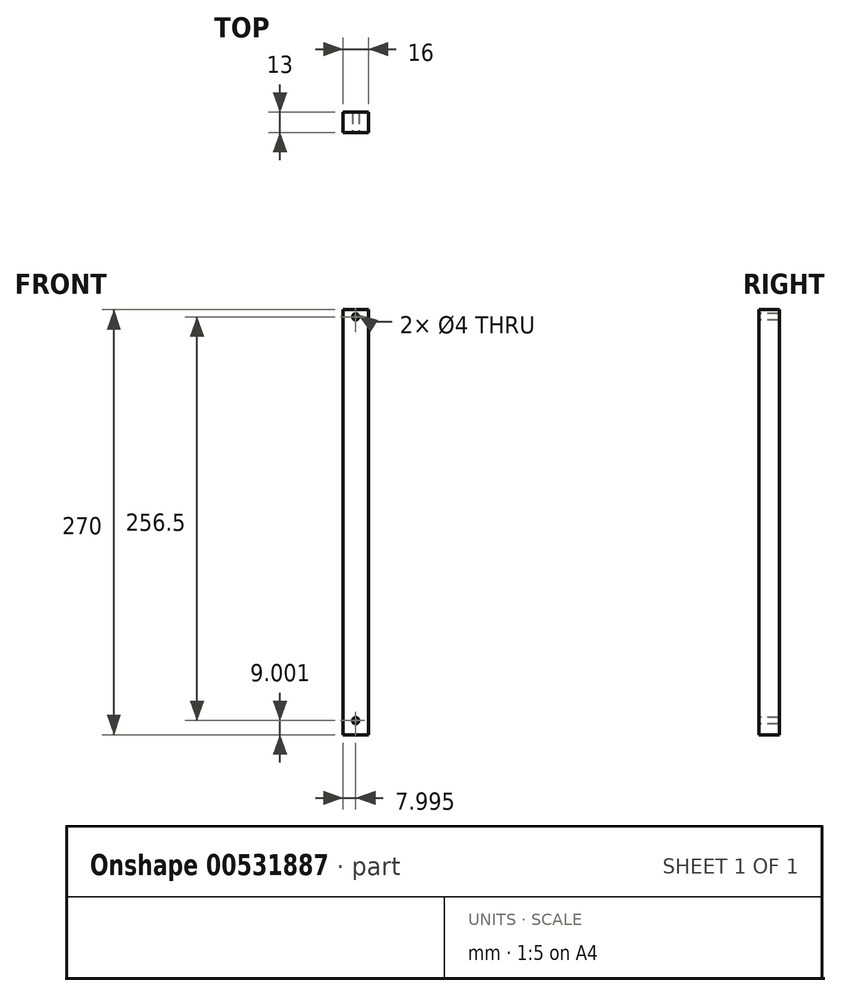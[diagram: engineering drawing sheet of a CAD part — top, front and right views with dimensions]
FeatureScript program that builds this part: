
annotation { "Feature Type Name" : "Feature", "Feature Type Description" : "" }
export const myFeature = defineFeature(function(context is Context, id is Id, definition is map)
    precondition{}
    {
        {
            var Q0;
            Q0=qCreatedBy(makeId("Front.planeOp"),FACE);
            var sketch = newSketch(context, id + "F0", { "sketchPlane" : qUnion([Q0])});
            skLineSegment(sketch, "E0.bottom", {"start": v(-46.2, 242.17) * mm, "end": v(-30.2, 242.17) * mm});
            skLineSegment(sketch, "E0.top", {"start": v(-46.2, -27.83) * mm, "end": v(-30.2, -27.83) * mm});
            skLineSegment(sketch, "E0.left", {"start": v(-46.2, 242.17) * mm, "end": v(-46.2, -27.83) * mm});
            skLineSegment(sketch, "E0.right", {"start": v(-30.2, 242.17) * mm, "end": v(-30.2, -27.83) * mm});
            skSolve(sketch);
        }
        {
            var Q0;
            Q0 = qSketchRegion(id + "F0", true);
            extrude(context, id + "F1", {"entities" : qUnion([Q0]), "depth" : 13 * mm, "offsetDistance" : 25 * mm});
        }
        {
            var Q0;
            Q0=makeQuery(id+"F1.opExtrude","CAP_FACE",FACE,{"disambiguationData":[OSD([sQuery(id+"F0.wireOp",EDGE,"E0.bottom"),sQuery(id+"F0.wireOp",EDGE,"E0.top"),sQuery(id+"F0.wireOp",EDGE,"E0.left"),sQuery(id+"F0.wireOp",EDGE,"E0.right")])],"isStart":false});
            var sketch = newSketch(context, id + "F2", { "sketchPlane" : qUnion([Q0])});
            skCircle(sketch, "E1", {"center": v(-38.2, -18.83) * mm, "radius": 2 * mm});
            skSolve(sketch);
        }
        {
            var Q0;
            Q0 = qSketchRegion(id + "F2", true);
            extrude(context, id + "F3", {"entities" : qUnion([Q0]), "operationType" : NewBodyOperationType.REMOVE, "oppositeDirection" : true, "depth" : 13 * mm, "offsetDistance" : 25 * mm});
        }
        {
            var Q0;
            Q0=makeQuery(id+"F1.opExtrude","CAP_FACE",FACE,{"disambiguationData":[OSD([sQuery(id+"F0.wireOp",EDGE,"E0.bottom"),sQuery(id+"F0.wireOp",EDGE,"E0.top"),sQuery(id+"F0.wireOp",EDGE,"E0.left"),sQuery(id+"F0.wireOp",EDGE,"E0.right")])],"isStart":false});
            var sketch = newSketch(context, id + "F4", { "sketchPlane" : qUnion([Q0])});
            skLineSegment(sketch, "E2", {"start": v(-46.2, 237.67) * mm, "end": v(-38.2, 237.67) * mm});
            skCircle(sketch, "E3", {"center": v(-38.2, 237.67) * mm, "radius": 2 * mm});
            skSolve(sketch);
        }
        {
            var Q0;
            Q0 = qSketchRegion(id + "F4", true);
            extrude(context, id + "F5", {"entities" : qUnion([Q0]), "operationType" : NewBodyOperationType.REMOVE, "oppositeDirection" : true, "depth" : 13 * mm, "offsetDistance" : 25 * mm});
        }
    });
